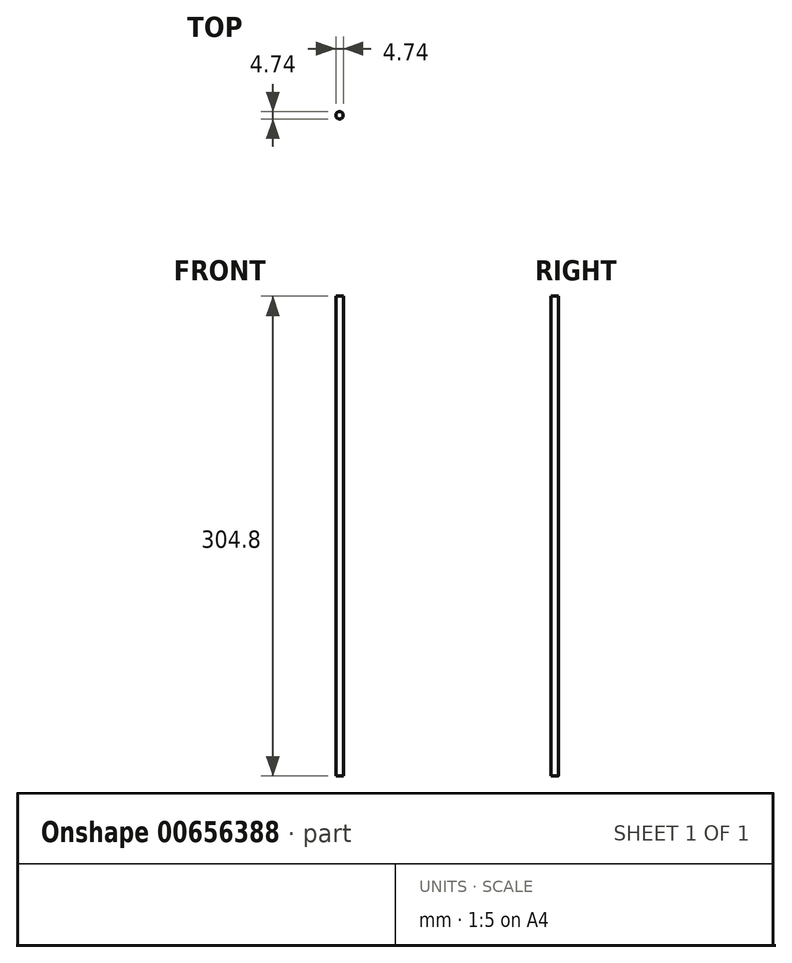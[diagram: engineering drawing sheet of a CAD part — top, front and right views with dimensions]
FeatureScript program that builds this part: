
annotation { "Feature Type Name" : "Feature", "Feature Type Description" : "" }
export const myFeature = defineFeature(function(context is Context, id is Id, definition is map)
    precondition{}
    {
        {
            var Q0;
            Q0=qCreatedBy(makeId("Top.planeOp"),FACE);
            var sketch = newSketch(context, id + "F0", { "sketchPlane" : qUnion([Q0])});
            skCircle(sketch, "E0", {"center": v(54.9, 71.84) * mm, "radius": 2.37 * mm});
            skSolve(sketch);
        }
        {
            var Q0;
            Q0 = qSketchRegion(id + "F0", true);
            extrude(context, id + "F1", {"entities" : qUnion([Q0]), "depth" : 304.8 * mm, "offsetDistance" : 25.4 * mm});
        }
    });
